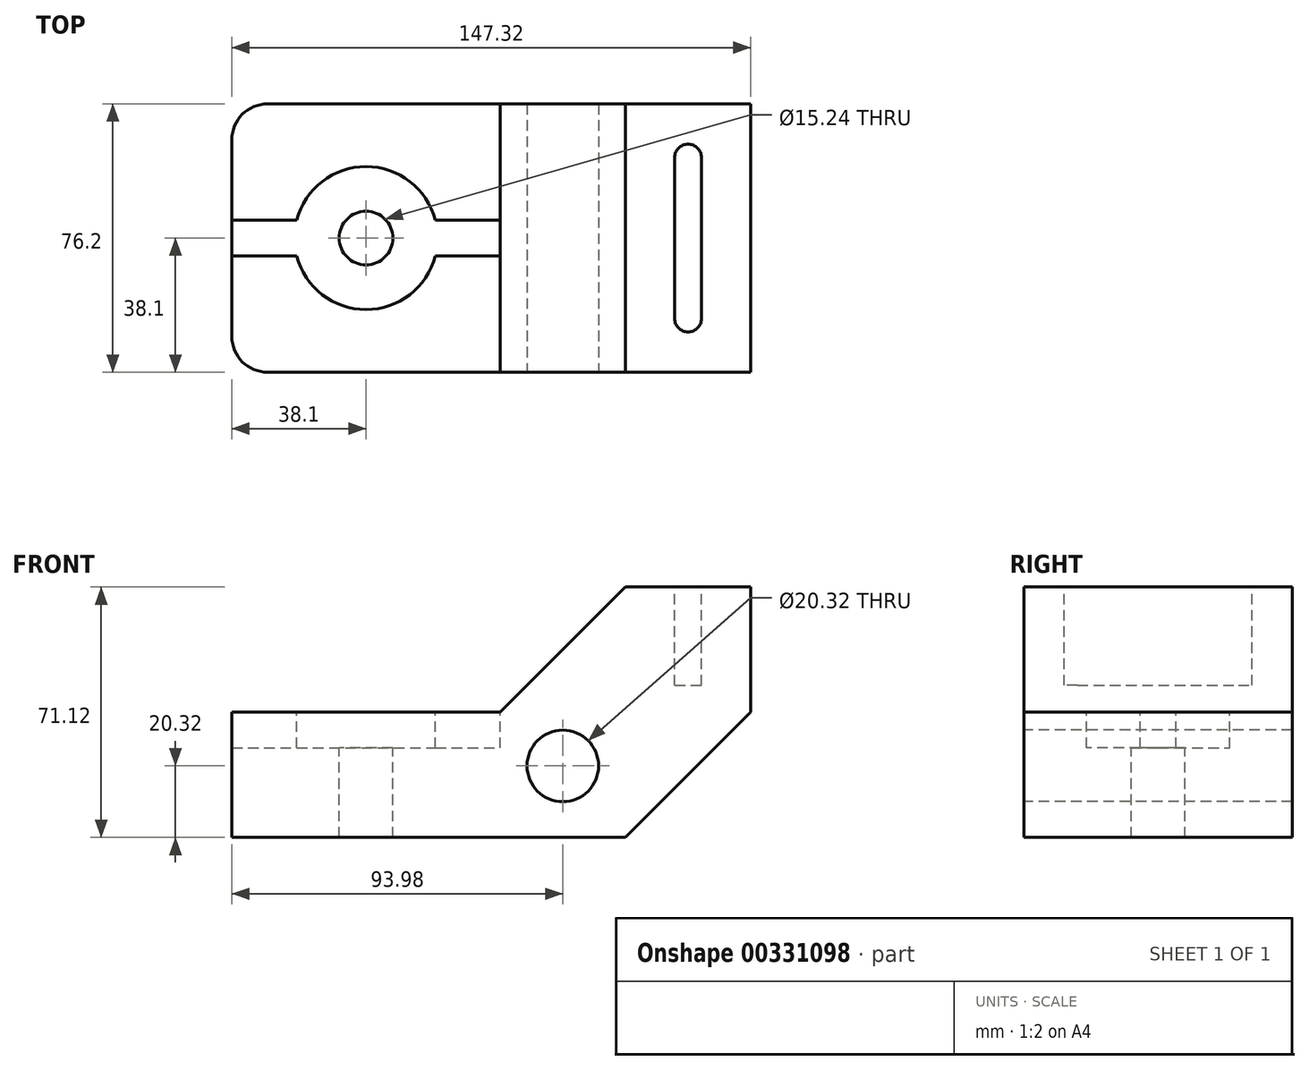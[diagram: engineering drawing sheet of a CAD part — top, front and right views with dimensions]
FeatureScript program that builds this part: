
annotation { "Feature Type Name" : "Feature", "Feature Type Description" : "" }
export const myFeature = defineFeature(function(context is Context, id is Id, definition is map)
    precondition{}
    {
        {
            var Q0;
            Q0=qCreatedBy(makeId("Front.planeOp"),FACE);
            var sketch = newSketch(context, id + "F0", { "sketchPlane" : qUnion([Q0])});
            skLineSegment(sketch, "E0", {"start": v(0, 0) * mm, "end": v(0, 35.56) * mm});
            skLineSegment(sketch, "E1", {"start": v(0, 35.56) * mm, "end": v(76.2, 35.56) * mm});
            skLineSegment(sketch, "E2", {"start": v(0, 0) * mm, "end": v(147.32, 0) * mm, "construction": true});
            skLineSegment(sketch, "E3", {"start": v(0, 0) * mm, "end": v(111.76, 0) * mm});
            skLineSegment(sketch, "E4", {"start": v(147.32, 0) * mm, "end": v(147.32, 71.12) * mm, "construction": true});
            skLineSegment(sketch, "E5", {"start": v(147.32, 71.12) * mm, "end": v(147.32, 35.56) * mm});
            skLineSegment(sketch, "E6", {"start": v(111.76, 0) * mm, "end": v(147.32, 35.56) * mm});
            skLineSegment(sketch, "E7", {"start": v(147.32, 71.12) * mm, "end": v(111.76, 71.12) * mm});
            skLineSegment(sketch, "E8", {"start": v(111.76, 71.12) * mm, "end": v(76.2, 35.56) * mm});
            skSolve(sketch);
        }
        {
            var Q0;
            Q0=makeQuery(id+"F0.imprint","IMPRINT",FACE,{"disambiguationData":[TD([[makeQuery(id+"F0.imprint","IMPRINT",EDGE,{"derivedFrom":sQuery(id+"F0.wireOp",EDGE,"E0")}),-1.0]])]});
            extrude(context, id + "F1", {"entities" : qUnion([Q0]), "oppositeDirection" : true, "depth" : 76.2 * mm});
        }
        {
            var Q0;
            Q0=makeQuery(id+"F1.opExtrude","SWEPT_FACE",FACE,{"disambiguationData":[OSD([sQuery(id+"F0.wireOp",EDGE,"E7")])]});
            var sketch = newSketch(context, id + "F2", { "sketchPlane" : qUnion([Q0])});
            skLineSegment(sketch, "E9", {"start": v(129.54, 15.24) * mm, "end": v(129.54, 60.96) * mm, "construction": true});
            skPoint(sketch, "E9.startSnap0", {"position": v(129.54, 0) * mm});
            skArc(sketch, "E10.0.startCap", {"start": v(133.35, 15.24) * mm, "mid": v(129.54, 11.43) * mm, "end": v(125.73, 15.24) * mm});
            skArc(sketch, "E10.0.endCap", {"start": v(125.73, 60.96) * mm, "mid": v(129.54, 64.77) * mm, "end": v(133.35, 60.96) * mm});
            skLineSegment(sketch, "E10.0.left", {"start": v(125.73, 15.24) * mm, "end": v(125.73, 60.96) * mm});
            skLineSegment(sketch, "E10.0.right", {"start": v(133.35, 15.24) * mm, "end": v(133.35, 60.96) * mm});
            skSolve(sketch);
        }
        {
            var Q0;
            Q0 = qSketchRegion(id + "F2", true);
            extrude(context, id + "F3", {"entities" : qUnion([Q0]), "operationType" : NewBodyOperationType.REMOVE, "oppositeDirection" : true, "depth" : 27.94 * mm});
        }
        {
            var Q0;
            Q0=makeQuery(id+"F0.imprint","IMPRINT",FACE,{"disambiguationData":[TD([[makeQuery(id+"F0.imprint","IMPRINT",EDGE,{"derivedFrom":sQuery(id+"F0.wireOp",EDGE,"E0")}),-1.0]])]});
            var sketch = newSketch(context, id + "F4", { "sketchPlane" : qUnion([Q0])});
            skCircle(sketch, "E11", {"center": v(93.98, 20.32) * mm, "radius": 10.16 * mm});
            skSolve(sketch);
        }
        {
            var Q0;
            Q0=makeQuery(id+"F4.imprint","IMPRINT",FACE,{"disambiguationData":[TD([[makeQuery(id+"F4.imprint","IMPRINT",EDGE,{"derivedFrom":sQuery(id+"F4.wireOp",EDGE,"E11")}),1.0]])]});
            var Q1;
            Q1=sQuery(id+"F4.wireOp",EDGE,"E11");
            extrude(context, id + "F5", {"entities" : qUnion([Q0]), "operationType" : NewBodyOperationType.REMOVE, "surfaceEntities" : qUnion([Q1]), "endBound" : BoundingType.THROUGH_ALL, "oppositeDirection" : true, "depth" : 25.4 * mm});
        }
        {
            var Q0;
            {var subQ2=sQuery(id+"F0.wireOp",EDGE,"E1");Q0=makeQuery(id+"FamMBtI0qrrW7aP_1.boolean.opBoolean","SPLIT",FACE,{"disambiguationData":[TD([makeQuery(id+"FamMBtI0qrrW7aP_1.opExtrude","SWEPT_FACE",FACE,{"disambiguationData":[OSD([sQuery(id+"F4HJX2g6tmivsij_1.wireOp",EDGE,"XuBJi9Rd-bP1s-Md4K-8pKo-xVkslWWFvv2a.bottom")])]})])],"derivedFrom":makeQuery(id+"F1.opExtrude","SWEPT_FACE",FACE,{"disambiguationData":[OSD([subQ2])]})});}
            var sketch = newSketch(context, id + "F6", { "sketchPlane" : qUnion([Q0])});
            skCircle(sketch, "E12", {"center": v(38.1, 38.1) * mm, "radius": 7.62 * mm});
            skCircle(sketch, "E13", {"center": v(38.1, 38.1) * mm, "radius": 20.32 * mm});
            skLineSegment(sketch, "E14", {"start": v(0, 43.18) * mm, "end": v(0, 33.02) * mm});
            skLineSegment(sketch, "E15", {"start": v(0, 38.1) * mm, "end": v(76.2, 38.1) * mm, "construction": true});
            skLineSegment(sketch, "E16", {"start": v(0, 43.18) * mm, "end": v(18.43, 43.18) * mm});
            skLineSegment(sketch, "E17", {"start": v(0, 33.02) * mm, "end": v(18.43, 33.02) * mm});
            skLineSegment(sketch, "E18", {"start": v(57.77, 43.18) * mm, "end": v(76.2, 43.18) * mm});
            skLineSegment(sketch, "E19", {"start": v(57.77, 33.02) * mm, "end": v(76.2, 33.02) * mm});
            skLineSegment(sketch, "E20", {"start": v(76.2, 33.02) * mm, "end": v(76.2, 43.18) * mm});
            skSolve(sketch);
        }
        {
            var Q0;
            Q0=makeQuery(id+"F6.imprint","IMPRINT",FACE,{"disambiguationData":[TD([[makeQuery(id+"F6.imprint","IMPRINT",EDGE,{"derivedFrom":sQuery(id+"F6.wireOp",EDGE,"E14")}),1.0]])]});
            var Q1;
            {var subQ0=sQuery(id+"F6.wireOp",EDGE,"E18");Q1=makeQuery(id+"F6.imprint","IMPRINT",FACE,{"disambiguationData":[TD([[makeQuery(id+"F6.imprint","IMPRINT",EDGE,{"derivedFrom":subQ0}),-1.0]])]});}
            extrude(context, id + "F7", {"entities" : qUnion([Q0, Q1]), "operationType" : NewBodyOperationType.REMOVE, "oppositeDirection" : true, "depth" : 10.16 * mm});
        }
        {
            var Q0;
            Q0=sQuery(id+"F6.wireOp",VERTEX,"E13.center");
            var Q1;
            Q1=makeQuery(id+"F1.opExtrude","SWEPT_BODY",BODY,{"disambiguationData":[OSD([sQuery(id+"F0.wireOp",EDGE,"E0"),sQuery(id+"F0.wireOp",EDGE,"E1"),sQuery(id+"F0.wireOp",EDGE,"E3"),sQuery(id+"F0.wireOp",EDGE,"E5"),sQuery(id+"F0.wireOp",EDGE,"E6"),sQuery(id+"F0.wireOp",EDGE,"E7"),sQuery(id+"F0.wireOp",EDGE,"E8")])]});
            hole(context, id + "F8", {"style" : HoleStyle.C_BORE, "endStyle" : HoleEndStyle.THROUGH, "holeDiameter" : 15.24 * mm, "cBoreDiameter" : 40.64 * mm, "cBoreDepth" : 10.16 * mm, "tappedDepth" : 12.7 * mm, "tapClearance" : 3, "locations" : qUnion([Q0]), "scope" : qUnion([Q1])});
        }
        {
            var Q0;
            Q0=makeQuery(id+"F1.opExtrude","CAP_EDGE",EDGE,{"disambiguationData":[OSD([sQuery(id+"F0.wireOp",EDGE,"E0")])],"isStart":true});
            var Q1;
            Q1=makeQuery(id+"F1.opExtrude","CAP_EDGE",EDGE,{"disambiguationData":[OSD([sQuery(id+"F0.wireOp",EDGE,"E0")])],"isStart":false});
            fillet(context, id + "F9", {"entities" : qUnion([Q0, Q1]), "radius" : 10.16 * mm, "tangentPropagation" : true, "allowEdgeOverflow" : false});
        }
    });
